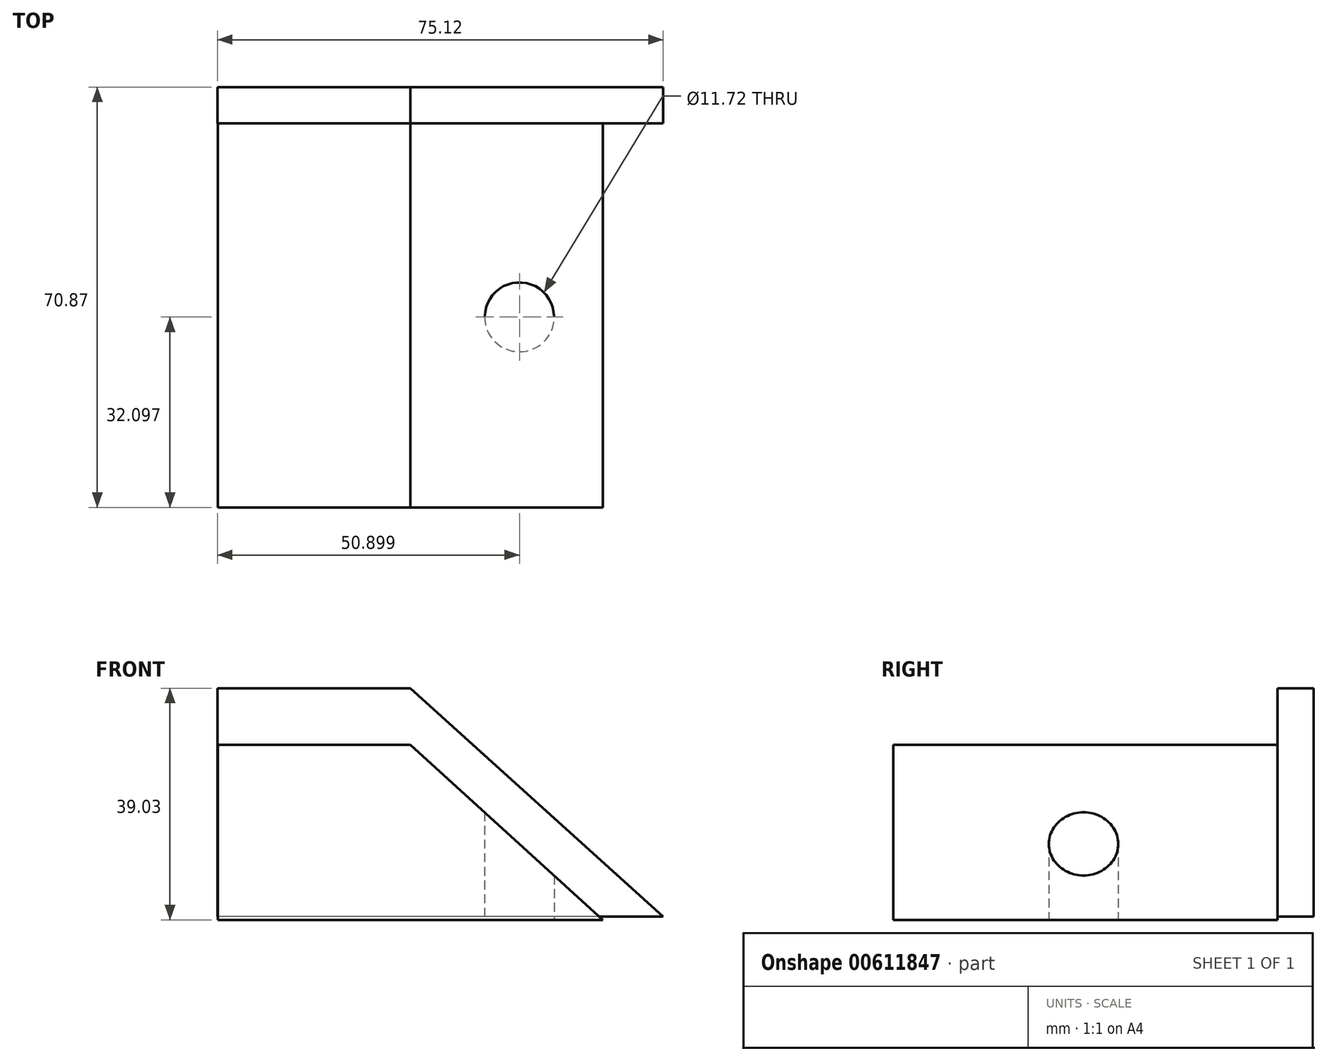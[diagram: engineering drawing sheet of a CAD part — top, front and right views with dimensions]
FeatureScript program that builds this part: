
annotation { "Feature Type Name" : "Feature", "Feature Type Description" : "" }
export const myFeature = defineFeature(function(context is Context, id is Id, definition is map)
    precondition{}
    {
        {
            var Q0;
            Q0=qCreatedBy(makeId("Front.planeOp"),FACE);
            var sketch = newSketch(context, id + "F0", { "sketchPlane" : qUnion([Q0])});
            skLineSegment(sketch, "E0.bottom", {"start": v(0, 14.75) * mm, "end": v(-32.46, 14.75) * mm});
            skLineSegment(sketch, "E0.top", {"start": v(32.46, -14.75) * mm, "end": v(-32.46, -14.75) * mm});
            skLineSegment(sketch, "E0.right", {"start": v(-32.46, 14.75) * mm, "end": v(-32.46, -14.75) * mm});
            skPoint(sketch, "E0.middle", {"position": v(0, 0) * mm});
            skLineSegment(sketch, "E1", {"start": v(0, 14.75) * mm, "end": v(32.46, -14.75) * mm});
            skPoint(sketch, "E0.left.start.orphan", {"position": v(32.46, 14.75) * mm});
            skSolve(sketch);
        }
        {
            var Q0;
            Q0 = qSketchRegion(id + "F0", true);
            extrude(context, id + "F1", {"entities" : qUnion([Q0]), "depth" : 64.77 * mm, "offsetDistance" : 25.4 * mm});
        }
        {
            var Q0;
            Q0=qCreatedBy(makeId("Front.planeOp"),FACE);
            var sketch = newSketch(context, id + "F2", { "sketchPlane" : qUnion([Q0])});
            skLineSegment(sketch, "E2", {"start": v(42.6, -14.2) * mm, "end": v(-32.52, -14.2) * mm});
            skLineSegment(sketch, "E3", {"start": v(-32.52, 24.28) * mm, "end": v(0, 24.28) * mm});
            skLineSegment(sketch, "E4", {"start": v(0, 24.28) * mm, "end": v(42.6, -14.2) * mm});
            skLineSegment(sketch, "E5", {"start": v(-32.52, 24.28) * mm, "end": v(-32.52, -14.2) * mm});
            skSolve(sketch);
        }
        {
            var Q0;
            Q0=makeQuery(id+"F2.imprint","IMPRINT",FACE,{"disambiguationData":[TD([[makeQuery(id+"F2.imprint","IMPRINT",EDGE,{"derivedFrom":sQuery(id+"F2.wireOp",EDGE,"E2")}),-1.0]])]});
            extrude(context, id + "F3", {"entities" : qUnion([Q0]), "operationType" : NewBodyOperationType.ADD, "oppositeDirection" : true, "depth" : 6.1 * mm, "offsetDistance" : 25.4 * mm});
        }
        {
            var Q0;
            Q0=makeQuery(id+"F1.opExtrude","SWEPT_FACE",FACE,{"disambiguationData":[OSD([sQuery(id+"F0.wireOp",EDGE,"E0.top")])]});
            var sketch = newSketch(context, id + "F4", { "sketchPlane" : qUnion([Q0])});
            skCircle(sketch, "E6", {"center": v(18.38, 32.67) * mm, "radius": 5.86 * mm});
            skSolve(sketch);
        }
        {
            var Q0;
            Q0=makeQuery(id+"F4.imprint","IMPRINT",FACE,{"disambiguationData":[TD([[makeQuery(id+"F4.imprint","IMPRINT",EDGE,{"derivedFrom":sQuery(id+"F4.wireOp",EDGE,"E6")}),1.0]])]});
            var Q1;
            Q1=sQuery(id+"F4.wireOp",EDGE,"E6");
            extrude(context, id + "F5", {"entities" : qUnion([Q0]), "operationType" : NewBodyOperationType.REMOVE, "surfaceEntities" : qUnion([Q1]), "oppositeDirection" : true, "depth" : 79.25 * mm, "offsetDistance" : 25.4 * mm});
        }
    });
